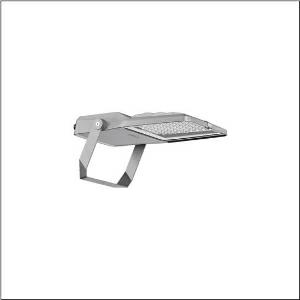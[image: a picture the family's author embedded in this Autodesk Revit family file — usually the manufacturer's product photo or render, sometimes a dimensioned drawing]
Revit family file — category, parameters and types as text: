
# Revit family: floodlight_fl_21_iq_mini___pl52_5xa7772b3d1a_2253
name_source: partatom
category: Lighting Fixtures
units: mm (PartAtom-declared; Revit-internal decimal feet)

## family parameters
Cut with Voids When Loaded = No
Host = Face
Light Source = No
Part Type = Normal
Room Calculation Point = No
Round Connector Dimension = Use Diameter
Shared = No

## types (1)
- --- (1 x LED, 5370 lm, 45.5 W, 3000K)
    Apparent Load = 46 VA
    CIE Flux Codes = 26 60 98 100 100
    Color Rendering = 80
    Color Temperature = 3000K
    Default Elevation = 1800 mm
    Description = Floodlight FL 21 iQ mini, floodlight, primary light control with lens, of PMMA, primary optical cover: protective disc, of toughened safety glass, transparent, light distribution: PL52, light emission: direct distribution, installation type: surface-mounted, LED, High Power LED, rated luminous flux: 5.370lm, luminous efficacy: 118lm/W, light colour: 830, colour temperature: 3000K, control gear: iQ Street-Remote/DALI, control: Street-Remote, Auto-Match, Temp-Guard, Night-Set, Smart-Wire, Desk-Remote (wireless, voltage-free reading and setting of iQ features in the workshop via application-optimized NFC function/RFID function), optimised constant luminous flux control (CLO 2.0), with terminal, 6-pole, mains connection: 220..240V, AC, 50/60Hz, start of lifetime: 46W, end of service life: 48W, reduction: 21W, luminaire housing, of diecast aluminium, powder-coated, Siteco® metallic grey (DB 702S), corrosivity category C5 mid according to DIN EN ISO 12944, suitable for swimming pools, chlorine-resistant, sealing non-destructively replaceable, mounting bracket, of steel, galvanised, powder-coated, Siteco® metallic grey (DB 702S), protection rating (complete): IP66, insulation class (complete): insulation class II (safety insulation), certification: CE, ENEC, VDE, protection symbol: D, impact resistance: IK08, permissible operating ambient temperature: -40..+40°C, permissible operating ambient temperature for outdoor applications: -40..+50°C, standard: DIN EN 12944, LABS conformity tested according to VDMA 24364:2018-05, packaging unit: 1 piece

Light Distribution: PL52
    Height = 70 mm
    Lamp = 1 x LED
    Lamp Light Flux = 5370 lm
    Lamp Power = 45.5 W
    Lamp count = 1
    Length = 485 mm
    Luminous efficacy = 118 lm/W
    Manufacturer = Siteco
    ModVariant = No
    Model = 5XA7772B3D1A
    Number of Poles = 1
    OnlyDefault = Yes
    Power Factor = 1
    Product Name = Floodlight FL 21 iQ mini | PL52
    Product group = floodlight | pylon annexe
    ProductGroupID = 6200
    Protection Class = Protection class II
    Protection Degree = IP 66
    RLX_Detail_Level = 1
    RLX_Emergency_Light_Flux = 0 lm
    RLX_Emergency_Type = 0
    RLX_Emergency_Type_DB = No
    RlxData = <blob elided: 96393 chars, md5=37bda146>
    Socket = socket
    Standby Power = 0 W
    System Light Flux = 5370 lm
    System Power = 46 W
    Type Comments = factory setting: luminous flux: 100 % | dim-lin: 254 | 463 mA
    Type Image = l_1006845.jpg
    URL = http://relux.com
    VarID = @adj_164808
    Voltage = 0 V
    Weight = 0.00 kg
    Width = 337 mm

## geometry (parser evidence)
native form markers: Blend x4, Sweep x11
no freeform markers — native parametric forms only
